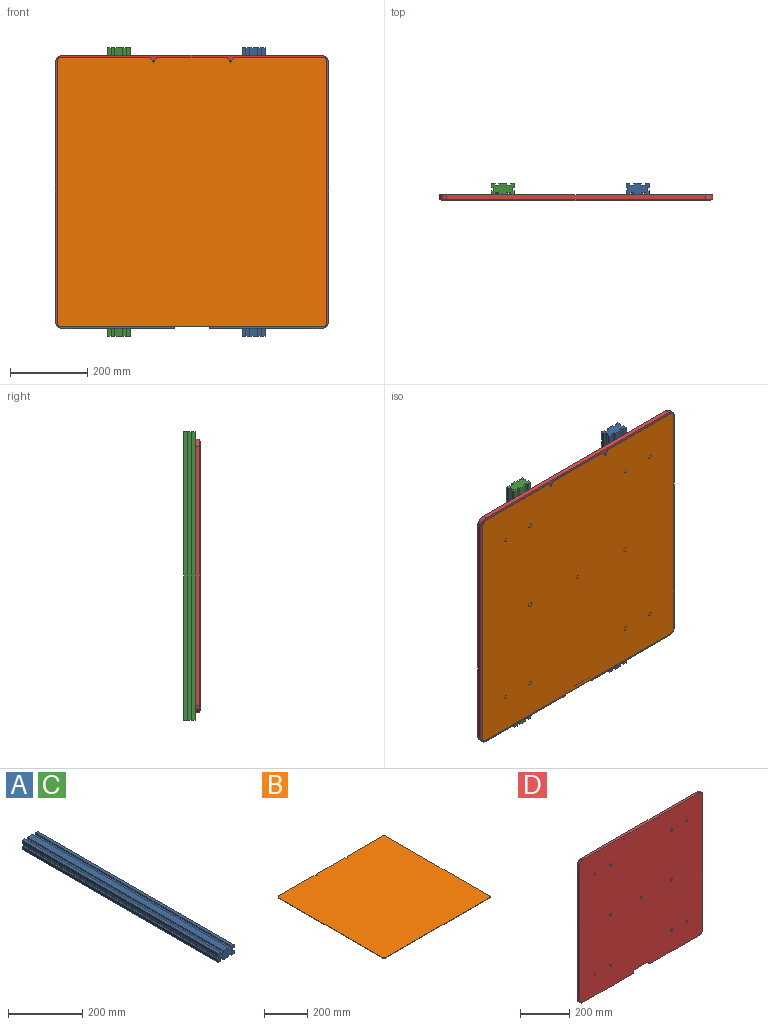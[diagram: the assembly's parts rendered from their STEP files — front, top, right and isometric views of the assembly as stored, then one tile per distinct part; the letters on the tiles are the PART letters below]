
ASSEMBLY  parts=4 mates=3
PART A: 30 faces, bbox 60x750x30 mm
  f0: plane 750x10mm, normal (0,0,1), area 7500mm2, adj f1,f27,f28,f29
  f1: plane 750x5mm, normal (1,0,0), area 3750mm2, adj f0,f2,f28,f29
  f2: plane 750x10mm, normal (0,0,1), area 7500mm2, adj f1,f3,f28,f29
  f3: plane 750x10mm, normal (-1,0,0), area 7500mm2, adj f2,f4,f28,f29
  f4: plane 750x5mm, normal (0,0,-1), area 3750mm2, adj f3,f5,f28,f29
  f5: plane 750x10mm, normal (-1,0,0), area 7500mm2, adj f4,f6,f28,f29
  f6: plane 750x5mm, normal (0,0,1), area 3750mm2, adj f5,f7,f28,f29
  f7: plane 750x10mm, normal (-1,0,0), area 7500mm2, adj f6,f8,f28,f29
  f8: plane 750x10mm, normal (0,0,-1), area 7500mm2, adj f7,f9,f28,f29
  f9: plane 750x5mm, normal (1,0,0), area 3750mm2, adj f8,f10,f28,f29
  f10: plane 750x10mm, normal (0,0,-1), area 7500mm2, adj f9,f11,f28,f29
  f11: plane 750x5mm, normal (-1,0,0), area 3750mm2, adj f10,f12,f28,f29
  f12: plane 750x20mm, normal (0,0,-1), area 15000mm2, adj f11,f13,f28,f29
  f13: plane 750x5mm, normal (1,0,0), area 3750mm2, adj f12,f14,f28,f29
  f14: plane 750x10mm, normal (0,0,-1), area 7500mm2, adj f13,f15,f28,f29
  f15: plane 750x5mm, normal (-1,0,0), area 3750mm2, adj f14,f16,f28,f29
  f16: plane 750x10mm, normal (0,0,-1), area 7500mm2, adj f15,f17,f28,f29
  f17: plane 750x10mm, normal (1,0,0), area 7500mm2, adj f16,f18,f28,f29
  f18: plane 750x5mm, normal (0,0,1), area 3750mm2, adj f17,f19,f28,f29
  f19: plane 750x10mm, normal (1,0,0), area 7500mm2, adj f18,f20,f28,f29
  f20: plane 750x5mm, normal (0,0,-1), area 3750mm2, adj f19,f21,f28,f29
  f21: plane 750x10mm, normal (1,0,0), area 7500mm2, adj f20,f22,f28,f29
  f22: plane 750x10mm, normal (0,0,1), area 7500mm2, adj f21,f23,f28,f29
  f23: plane 750x5mm, normal (-1,0,0), area 3750mm2, adj f22,f24,f28,f29
  f24: plane 750x10mm, normal (0,0,1), area 7500mm2, adj f23,f25,f28,f29
  f25: plane 750x5mm, normal (1,0,0), area 3750mm2, adj f24,f26,f28,f29
  f26: plane 750x20mm, normal (0,0,1), area 15000mm2, adj f25,f27,f28,f29
  f27: plane 750x5mm, normal (-1,0,0), area 3750mm2, adj f0,f26,f28,f29
  f28: plane 60x30mm, normal (0,-1,0), area 1500mm2, adj f0,f1,f2,f3,f4,f5,f6,f7
  f29: plane 60x30mm, normal (0,1,0), area 1500mm2, adj f0,f1,f2,f3,f4,f5,f6,f7
PART B: 18 faces, bbox 700x700x2 mm
  f0: cylinder r=2.5mm len=4.33mm, axis (0,0,-1), area 10.5mm2, adj f1,f15,f16,f17
  f1: plane 11.25x6.5mm, normal (0.87,0.5,0), area 26mm2, adj f0,f2,f16,f17
  f2: plane 231.34x2mm, normal (0,1,0), area 462.7mm2, adj f1,f3,f16,f17
  f3: cylinder r=10mm len=10mm, axis (0,0,-1), area 31.4mm2, adj f2,f4,f16,f17
  f4: plane 680x2mm, normal (-1,0,0), area 1360mm2, adj f3,f5,f16,f17
  f5: cylinder r=10mm len=10mm, axis (0,0,-1), area 31.4mm2, adj f4,f6,f16,f17
  f6: plane 680x2mm, normal (0,-1,0), area 1360mm2, adj f5,f7,f16,f17
  f7: cylinder r=10mm len=10mm, axis (0,0,-1), area 31.4mm2, adj f6,f8,f16,f17
  f8: plane 680x2mm, normal (1,0,0), area 1360mm2, adj f7,f9,f16,f17
  f9: cylinder r=10mm len=10mm, axis (0,0,-1), area 31.4mm2, adj f8,f10,f16,f17
  f10: plane 231.34x2mm, normal (0,1,0), area 462.7mm2, adj f9,f11,f16,f17
  f11: plane 11.25x6.5mm, normal (-0.87,0.5,0), area 26mm2, adj f10,f12,f16,f17
  f12: cylinder r=2.5mm len=4.33mm, axis (0,0,-1), area 10.5mm2, adj f11,f13,f16,f17
  f13: plane 11.25x6.5mm, normal (0.87,0.5,0), area 26mm2, adj f12,f14,f16,f17
  f14: plane 182.68x2mm, normal (0,1,0), area 365.4mm2, adj f13,f15,f16,f17
  f15: plane 11.25x6.5mm, normal (-0.87,0.5,0), area 26mm2, adj f0,f14,f16,f17
  f16: plane 700x700mm, normal (0,0,1), area 489662.9mm2, adj f0,f1,f2,f3,f4,f5,f6,f7
  f17: plane 700x700mm, normal (0,0,-1), area 489662.9mm2, adj f0,f1,f2,f3,f4,f5,f6,f7
PART C: same geometry as A
PART D: 48 faces, bbox 710x12x710 mm
  f0: plane 285x12mm, normal (0,0,-1), area 3420mm2, adj f8,f9,f31,f34
  f1: plane 12x5mm, normal (1,0,0), area 60mm2, adj f8,f9,f34,f36
  f2: plane 80x12mm, normal (0,0,-1), area 960mm2, adj f8,f9,f36,f37
  f3: plane 12x5mm, normal (-1,0,0), area 60mm2, adj f8,f9,f35,f37
  f4: plane 285x12mm, normal (0,0,-1), area 3420mm2, adj f8,f9,f28,f35
  f5: plane 670x12mm, normal (1,0,0), area 8040mm2, adj f8,f9,f28,f29
  f6: plane 670x12mm, normal (0,0,1), area 8040mm2, adj f8,f9,f29,f30
  f7: plane 670x12mm, normal (-1,0,0), area 8040mm2, adj f8,f9,f30,f31
  f8: plane 710x710mm, normal (0,-1,0), area 501296.1mm2, adj f0,f1,f2,f3,f4,f5,f6,f7
  f9: plane 710x710mm, normal (0,1,0), area 501896.1mm2, adj f0,f1,f2,f3,f4,f5,f6,f7
  f10: cylinder r=5mm len=10mm, axis (0,-1,0), area 188.5mm2, adj f9,f11
  f11: plane 12x12mm, normal (0,-1,0), area 34.6mm2, adj f10,f12
  f12: cylinder r=6mm len=12mm, axis (0,-1,0), area 226.2mm2, adj f8,f11
  f13: cylinder r=5mm len=10mm, axis (0,-1,0), area 188.5mm2, adj f9,f14
  f14: plane 12x12mm, normal (0,-1,0), area 34.6mm2, adj f13,f15
  f15: cylinder r=6mm len=12mm, axis (0,-1,0), area 226.2mm2, adj f8,f14
  f16: cylinder r=5mm len=10mm, axis (0,-1,0), area 188.5mm2, adj f9,f17
  f17: plane 12x12mm, normal (0,-1,0), area 34.6mm2, adj f16,f18
  f18: cylinder r=6mm len=12mm, axis (0,-1,0), area 226.2mm2, adj f8,f17
  f19: cylinder r=5mm len=10mm, axis (0,-1,0), area 188.5mm2, adj f9,f20
  f20: plane 12x12mm, normal (0,-1,0), area 34.6mm2, adj f19,f21
  f21: cylinder r=6mm len=12mm, axis (0,-1,0), area 226.2mm2, adj f8,f20
  f22: cylinder r=5mm len=10mm, axis (0,-1,0), area 188.5mm2, adj f9,f23
  f23: plane 12x12mm, normal (0,-1,0), area 34.6mm2, adj f22,f24
  f24: cylinder r=6mm len=12mm, axis (0,-1,0), area 226.2mm2, adj f8,f23
  f25: cylinder r=5mm len=10mm, axis (0,-1,0), area 188.5mm2, adj f9,f26
  f26: plane 12x12mm, normal (0,-1,0), area 34.6mm2, adj f25,f27
  f27: cylinder r=6mm len=12mm, axis (0,-1,0), area 226.2mm2, adj f8,f26
  f28: cylinder r=20mm len=20mm, axis (0,1,0), area 377mm2, adj f4,f5,f8,f9
  f29: cylinder r=20mm len=20mm, axis (0,-1,0), area 377mm2, adj f5,f6,f8,f9
  f30: cylinder r=20mm len=20mm, axis (0,1,0), area 377mm2, adj f6,f7,f8,f9
  f31: cylinder r=20mm len=20mm, axis (0,-1,0), area 377mm2, adj f0,f7,f8,f9
  f32: cylinder r=2.5mm len=12mm, axis (0,-1,0), area 188.5mm2, adj f8,f9
  f33: cylinder r=2.5mm len=12mm, axis (0,-1,0), area 188.5mm2, adj f8,f9
  f34: cylinder r=5mm len=12mm, axis (0,1,0), area 94.2mm2, adj f0,f1,f8,f9
  f35: cylinder r=5mm len=12mm, axis (0,-1,0), area 94.2mm2, adj f3,f4,f8,f9
  f36: cylinder r=5mm len=12mm, axis (0,-1,0), area 94.2mm2, adj f1,f2,f8,f9
  f37: cylinder r=5mm len=12mm, axis (0,1,0), area 94.2mm2, adj f2,f3,f8,f9
  f38: cone r=0mm half-angle=59deg, axis (0,-1,0), area 91.6mm2, adj f39
  f39: cylinder r=5mm len=10mm, axis (0,-1,0), area 157.1mm2, adj f8,f38
  f40: cone r=0mm half-angle=59deg, axis (0,-1,0), area 91.6mm2, adj f41
  f41: cylinder r=5mm len=10mm, axis (0,-1,0), area 157.1mm2, adj f8,f40
  f42: cone r=0mm half-angle=59deg, axis (0,-1,0), area 91.6mm2, adj f43
  f43: cylinder r=5mm len=10mm, axis (0,-1,0), area 157.1mm2, adj f8,f42
  f44: cone r=0mm half-angle=59deg, axis (0,-1,0), area 91.6mm2, adj f45
  f45: cylinder r=5mm len=10mm, axis (0,-1,0), area 157.1mm2, adj f8,f44
  f46: cone r=0mm half-angle=59deg, axis (0,-1,0), area 91.6mm2, adj f47
  f47: cylinder r=5mm len=10mm, axis (0,-1,0), area 157.1mm2, adj f8,f46
PLACE A rot(axis=(-1,0,0),90deg) t=(160,15,-375)mm
PLACE B rot(axis=(1,0,0),90deg) t=(0,-12,0)mm
PLACE C rot(axis=(1,0,0),90deg) t=(-190,15,375)mm
PLACE D at identity fixed
MATE fastened D.f13 <-> A.f16  axis (0,1,0) through (175,0,0)mm
MATE fastened D.f33 <-> B.f0  axis (0,-1,0) through (-100,-12,340)mm
MATE fastened D.f25 <-> C.f22  axis (0,1,0) through (-175,0,0)mm
